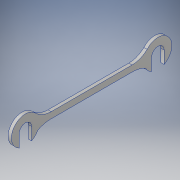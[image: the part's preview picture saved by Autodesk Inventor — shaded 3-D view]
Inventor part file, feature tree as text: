
AUTODESK INVENTOR PART (.ipt)
format: ipt  version: 2018 (Build 220112000, 112)  size: 120,832 bytes
history: native  units: in
note: dims shown in document units (in); Inventor stores cm internally (conversion verified against a paired STEP export)
features: extrude x1, sketch x1
ambient origin geometry x8: Origin, YZ Plane, XZ Plane, XY Plane, X Axis, Y Axis, Z Axis, Center Point
bodies: Body1 (feature_tree)
feature tree (2):
  extrude  "Extrusion2"  Depth=0.077in
  sketch  "Sketch1"  dims[d0=0.173in d10=0.25in d11=0.077in d12=0.02in d13=0.0in]
